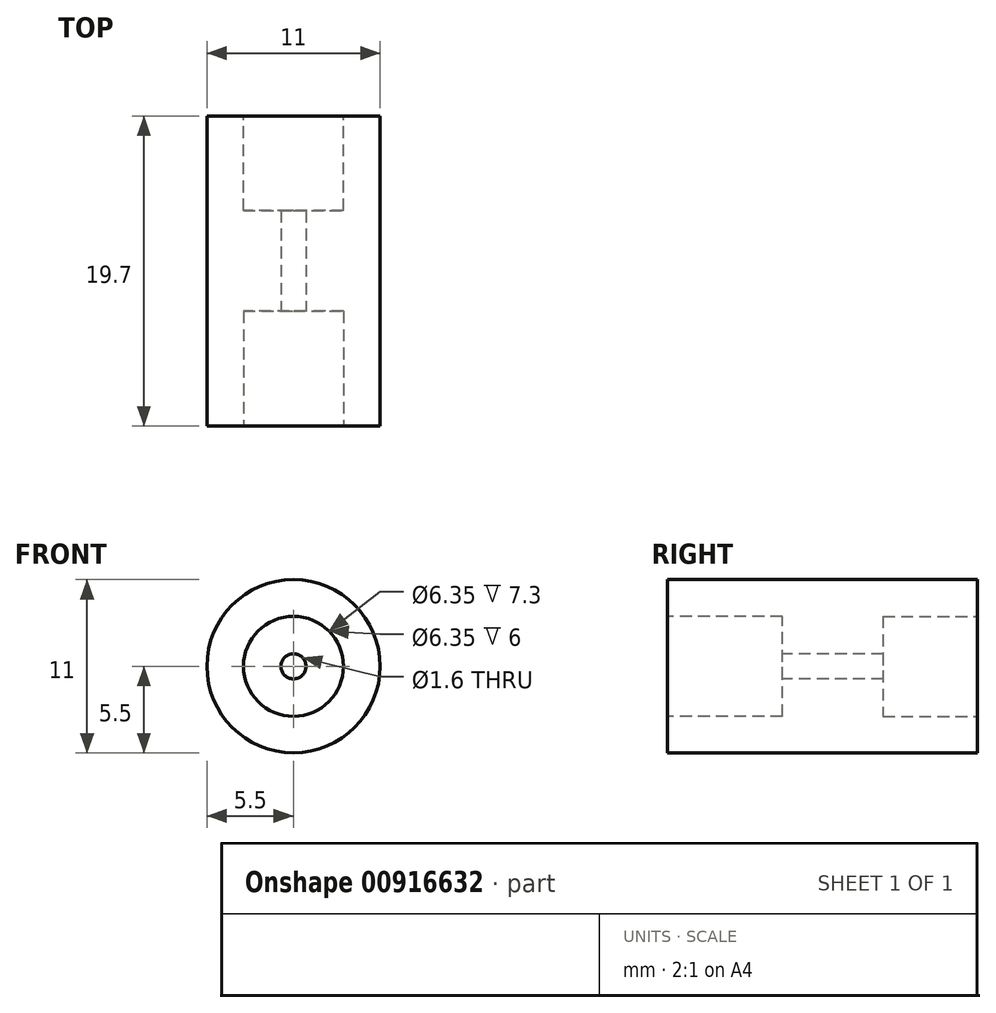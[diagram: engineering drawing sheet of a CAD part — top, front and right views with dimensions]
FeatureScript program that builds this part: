
annotation { "Feature Type Name" : "Feature", "Feature Type Description" : "" }
export const myFeature = defineFeature(function(context is Context, id is Id, definition is map)
    precondition{}
    {
        {
            var Q0;
            Q0=qCreatedBy(makeId("Front.planeOp"),FACE);
            var sketch = newSketch(context, id + "F0", { "sketchPlane" : qUnion([Q0])});
            skCircle(sketch, "E0", {"center": v(0, 0) * mm, "radius": 5.5 * mm});
            skSolve(sketch);
        }
        {
            var Q0;
            Q0=makeQuery(id+"F0.imprint","IMPRINT",FACE,{"disambiguationData":[TD([[makeQuery(id+"F0.imprint","IMPRINT",EDGE,{"derivedFrom":sQuery(id+"F0.wireOp",EDGE,"E0")}),1.0]])]});
            extrude(context, id + "F1", {"entities" : qUnion([Q0]), "depth" : 19.7 * mm, "offsetDistance" : 25 * mm});
        }
        {
            var Q0;
            Q0=makeQuery(id+"F1.opExtrude","CAP_FACE",FACE,{"disambiguationData":[OSD([sQuery(id+"F0.wireOp",EDGE,"E0")])],"isStart":false});
            var sketch = newSketch(context, id + "F2", { "sketchPlane" : qUnion([Q0])});
            skCircle(sketch, "E1", {"center": v(0, 0) * mm, "radius": 3.17 * mm});
            skSolve(sketch);
        }
        {
            var Q0;
            Q0=makeQuery(id+"F2.imprint","IMPRINT",FACE,{"disambiguationData":[TD([[makeQuery(id+"F2.imprint","IMPRINT",EDGE,{"derivedFrom":sQuery(id+"F2.wireOp",EDGE,"E1")}),1.0]])]});
            extrude(context, id + "F3", {"entities" : qUnion([Q0]), "operationType" : NewBodyOperationType.REMOVE, "oppositeDirection" : true, "depth" : 7.3 * mm, "offsetDistance" : 25 * mm});
        }
        {
            var Q0;
            Q0=makeQuery(id+"F3.boolean.opBoolean","COPY",FACE,{"derivedFrom":makeQuery(id+"F3.opExtrude","CAP_FACE",FACE,{"disambiguationData":[OSD([sQuery(id+"F2.wireOp",EDGE,"E1")])],"isStart":false})});
            var sketch = newSketch(context, id + "F4", { "sketchPlane" : qUnion([Q0])});
            skCircle(sketch, "E2", {"center": v(0, 0) * mm, "radius": 0.8 * mm});
            skSolve(sketch);
        }
        {
            var Q0;
            Q0=makeQuery(id+"F1.opExtrude","CAP_FACE",FACE,{"disambiguationData":[OSD([sQuery(id+"F0.wireOp",EDGE,"E0")])],"isStart":true});
            var sketch = newSketch(context, id + "F5", { "sketchPlane" : qUnion([Q0])});
            skCircle(sketch, "E3", {"center": v(0, 0) * mm, "radius": 3.17 * mm});
            skSolve(sketch);
        }
        {
            var Q0;
            Q0=makeQuery(id+"F5.imprint","IMPRINT",FACE,{"disambiguationData":[TD([[makeQuery(id+"F5.imprint","IMPRINT",EDGE,{"derivedFrom":sQuery(id+"F5.wireOp",EDGE,"E3")}),1.0]])]});
            extrude(context, id + "F6", {"entities" : qUnion([Q0]), "operationType" : NewBodyOperationType.REMOVE, "oppositeDirection" : true, "depth" : 6 * mm, "offsetDistance" : 25 * mm});
        }
        {
            var Q0;
            Q0=makeQuery(id+"F4.imprint","IMPRINT",FACE,{"disambiguationData":[TD([[makeQuery(id+"F4.imprint","IMPRINT",EDGE,{"derivedFrom":sQuery(id+"F4.wireOp",EDGE,"E2")}),1.0]])]});
            extrude(context, id + "F7", {"entities" : qUnion([Q0]), "operationType" : NewBodyOperationType.REMOVE, "endBound" : BoundingType.THROUGH_ALL, "oppositeDirection" : true, "depth" : 25 * mm, "offsetDistance" : 25 * mm});
        }
    });
